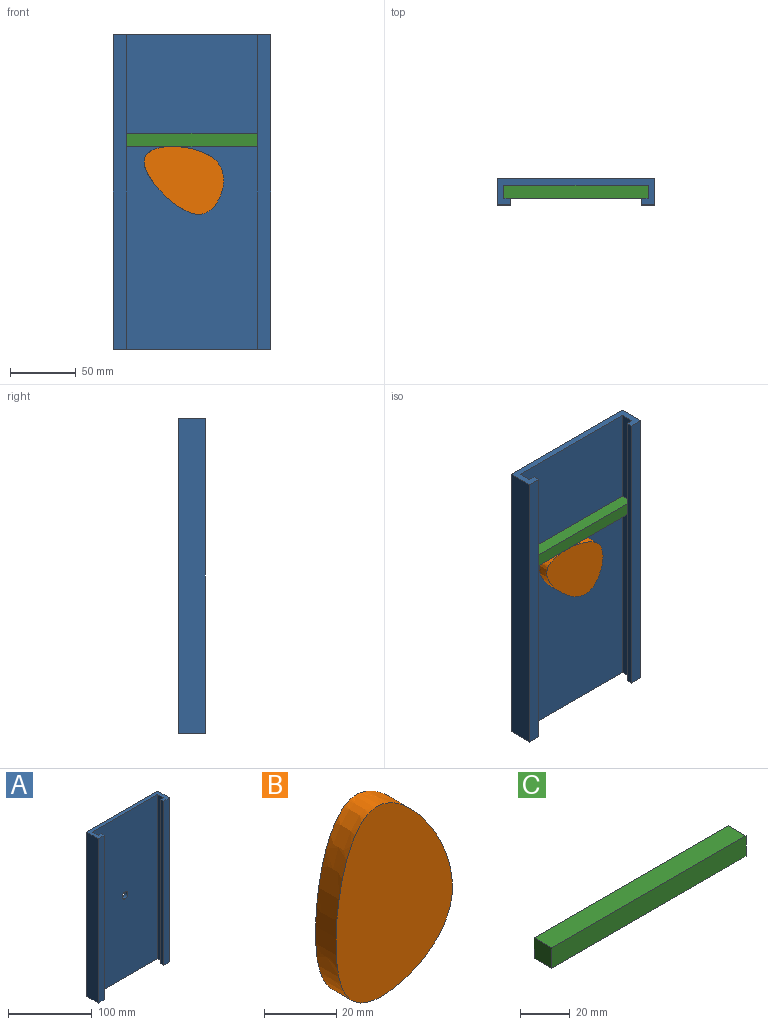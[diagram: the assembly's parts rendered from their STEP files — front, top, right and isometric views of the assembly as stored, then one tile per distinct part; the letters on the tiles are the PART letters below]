
ASSEMBLY  parts=3 mates=2
PART A: 15 faces, bbox 120x20x240 mm
  f0: plane 240x5mm, normal (1,0,0), area 1200mm2, adj f1,f3,f8,f13
  f1: plane 120x20mm, normal (0,0,-1), area 800mm2, adj f0,f2,f4,f5,f6,f7,f8,f9
  f2: plane 240x5mm, normal (-1,0,0), area 1200mm2, adj f1,f3,f6,f11
  f3: plane 120x20mm, normal (0,0,1), area 800mm2, adj f0,f2,f4,f5,f6,f7,f8,f9
  f4: plane 240x110mm, normal (0,-1,0), area 26321.5mm2, adj f1,f3,f5,f7,f14
  f5: plane 240x10mm, normal (-1,0,0), area 2400mm2, adj f1,f3,f4,f6
  f6: plane 240x5mm, normal (0,1,0), area 1200mm2, adj f1,f2,f3,f5
  f7: plane 240x10mm, normal (1,0,0), area 2400mm2, adj f1,f3,f4,f8
  f8: plane 240x5mm, normal (0,1,0), area 1200mm2, adj f0,f1,f3,f7
  f9: plane 240x120mm, normal (0,1,0), area 28721.5mm2, adj f1,f3,f10,f12,f14
  f10: plane 240x20mm, normal (1,0,0), area 4800mm2, adj f1,f3,f9,f11
  f11: plane 240x10mm, normal (0,-1,0), area 2400mm2, adj f1,f2,f3,f10
  f12: plane 240x20mm, normal (-1,0,0), area 4800mm2, adj f1,f3,f9,f13
  f13: plane 240x10mm, normal (0,-1,0), area 2400mm2, adj f0,f1,f3,f12
  f14: cylinder r=5mm len=10mm, axis (0,-1,0), area 157.1mm2, adj f4,f9
PART B: 5 faces, bbox 51x15x69 mm
  f0: plane 10x10mm, normal (0,1,0), area 78.5mm2, adj f1
  f1: cylinder r=5mm len=10mm, axis (0,-1,0), area 219.9mm2, adj f0,f4
  f2: extruded ~65.1x45.46mm, area 1405.8mm2, adj f3,f4
  f3: plane 69.02x51.05mm, normal (0,-1,0), area 2271.9mm2, adj f2
  f4: plane 69.02x51.05mm, normal (0,1,0), area 2193.4mm2, adj f1,f2
PART C: 6 faces, bbox 110x10x10 mm
  f0: plane 10x10mm, normal (1,0,0), area 100mm2, adj f1,f2,f4,f5
  f1: plane 110x10mm, normal (0,0,1), area 1100mm2, adj f0,f3,f4,f5
  f2: plane 110x10mm, normal (0,0,-1), area 1100mm2, adj f0,f3,f4,f5
  f3: plane 10x10mm, normal (-1,0,0), area 100mm2, adj f1,f2,f4,f5
  f4: plane 110x10mm, normal (0,1,0), area 1100mm2, adj f0,f1,f2,f3
  f5: plane 110x10mm, normal (0,-1,0), area 1100mm2, adj f0,f1,f2,f3
PLACE A at identity fixed
PLACE B rot(axis=(0,-1,0),51.5deg) t=(74.77,0,93.86)mm
PLACE C t=(0,0,-75.32)mm
MATE slider A.f3 <-> C.f1  axis (0,0,1) through (-55,2,120)mm
MATE revolute A.f14 <-> B.f1  axis (0,1,0) through (0,7,0)mm
